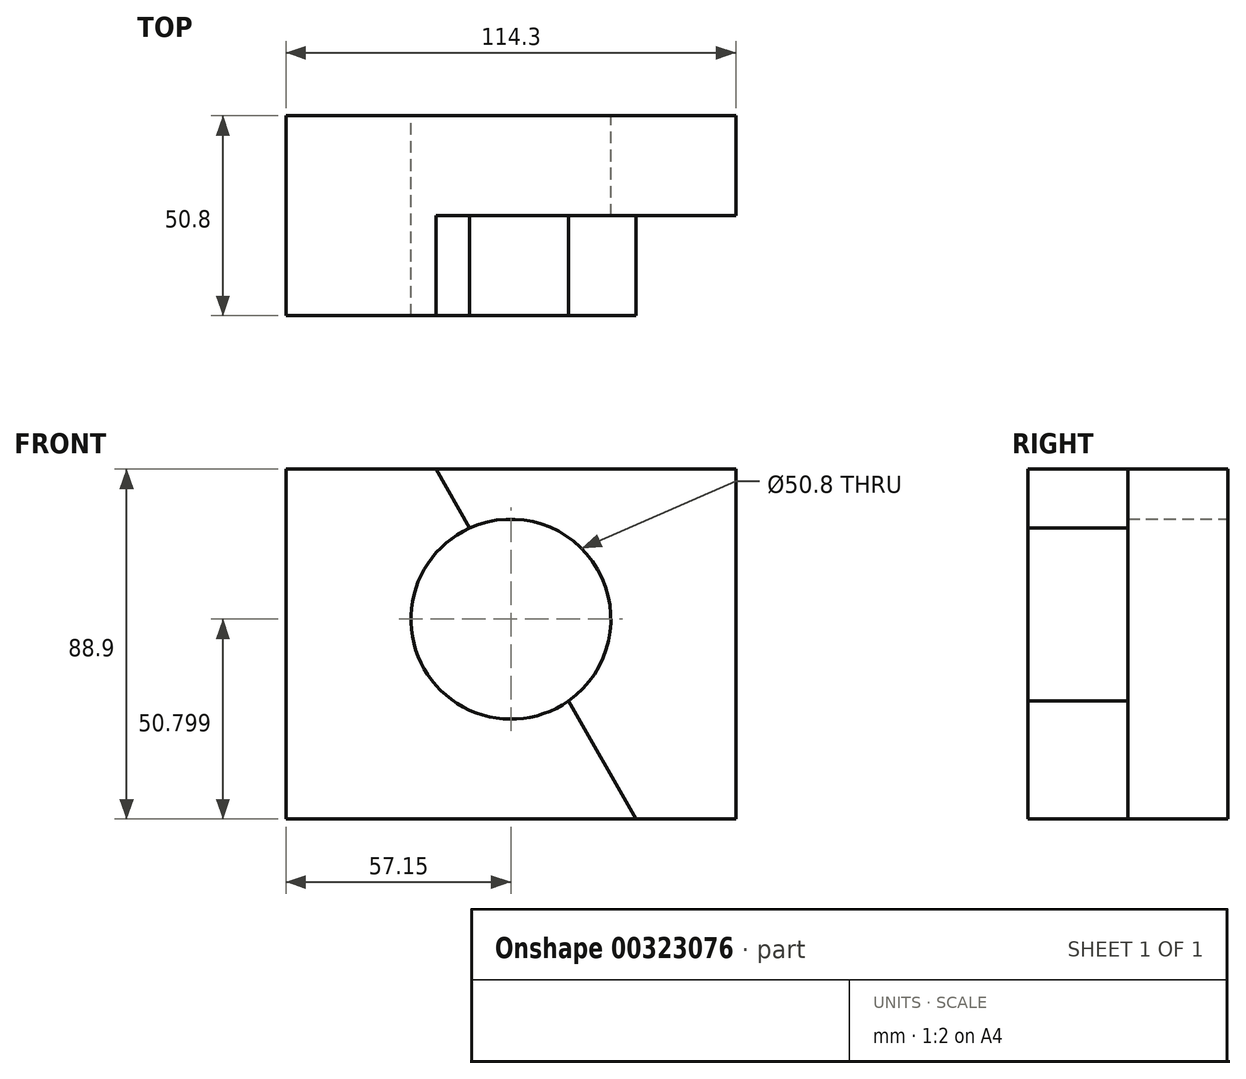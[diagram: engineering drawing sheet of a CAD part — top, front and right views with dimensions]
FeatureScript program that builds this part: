
annotation { "Feature Type Name" : "Feature", "Feature Type Description" : "" }
export const myFeature = defineFeature(function(context is Context, id is Id, definition is map)
    precondition{}
    {
        {
            var Q0;
            Q0=qCreatedBy(makeId("Front.planeOp"),FACE);
            var sketch = newSketch(context, id + "F0", { "sketchPlane" : qUnion([Q0])});
            skLineSegment(sketch, "E0.bottom", {"start": v(-65.5, 35.99) * mm, "end": v(48.8, 35.99) * mm});
            skLineSegment(sketch, "E0.top", {"start": v(-65.5, -52.91) * mm, "end": v(48.8, -52.91) * mm});
            skLineSegment(sketch, "E0.left", {"start": v(-65.5, 35.99) * mm, "end": v(-65.5, -52.91) * mm});
            skLineSegment(sketch, "E0.right", {"start": v(48.8, 35.99) * mm, "end": v(48.8, -52.91) * mm});
            skCircle(sketch, "E1", {"center": v(-8.35, -2.11) * mm, "radius": 25.4 * mm});
            skSolve(sketch);
        }
        {
            var Q0;
            Q0=makeQuery(id+"F0.imprint","IMPRINT",FACE,{"disambiguationData":[TD([[makeQuery(id+"F0.imprint","IMPRINT",EDGE,{"derivedFrom":sQuery(id+"F0.wireOp",EDGE,"E0.bottom")}),-1.0]])]});
            extrude(context, id + "F1", {"entities" : qUnion([Q0]), "depth" : 50.8 * mm});
        }
        {
            var Q0;
            Q0=makeQuery(id+"F1.opExtrude","CAP_FACE",FACE,{"disambiguationData":[OSD([sQuery(id+"F0.wireOp",EDGE,"E0.bottom"),sQuery(id+"F0.wireOp",EDGE,"E0.top"),sQuery(id+"F0.wireOp",EDGE,"E0.left"),sQuery(id+"F0.wireOp",EDGE,"E0.right"),sQuery(id+"F0.wireOp",EDGE,"E1")])],"isStart":false});
            var sketch = newSketch(context, id + "F2", { "sketchPlane" : qUnion([Q0])});
            skLineSegment(sketch, "E2", {"start": v(-65.5, 35.99) * mm, "end": v(-27.4, 35.99) * mm});
            skLineSegment(sketch, "E3", {"start": v(48.8, -52.91) * mm, "end": v(23.4, -52.91) * mm});
            skLineSegment(sketch, "E4", {"start": v(-27.4, 35.99) * mm, "end": v(23.4, -52.91) * mm});
            skSolve(sketch);
        }
        {
            var Q0;
            {var subQ4=sQuery(id+"F2.wireOp",EDGE,"E3");Q0=makeQuery(id+"F2.imprint","IMPRINT",FACE,{"disambiguationData":[TD([[makeQuery(id+"F2.imprint","IMPRINT",EDGE,{"derivedFrom":subQ4}),1.0]])]});}
            extrude(context, id + "F3", {"entities" : qUnion([Q0]), "operationType" : NewBodyOperationType.REMOVE, "oppositeDirection" : true, "depth" : 25.4 * mm});
        }
    });
